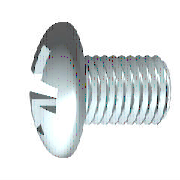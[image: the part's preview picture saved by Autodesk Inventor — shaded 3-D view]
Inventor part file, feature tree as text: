
AUTODESK INVENTOR PART (.ipt)
format: ipt  version: 2020 (Build 240168000, 168)  size: 274,432 bytes
history: native  units: mm (DEFAULTED — no unit token found)
features: other x2, plane x2, extrude x1
ambient origin geometry x7: Origin, YZ Plane, XZ Plane, X Axis, Y Axis, Z Axis, Center Point
bodies: Solid1 (feature_tree)
feature tree (5):
  other  "Базовый элемент"
  plane  "Work Plane1"
  extrude  "Паз"  Depth=2.0mm
  other  "Вырез"
  plane  "Work Plane3"
